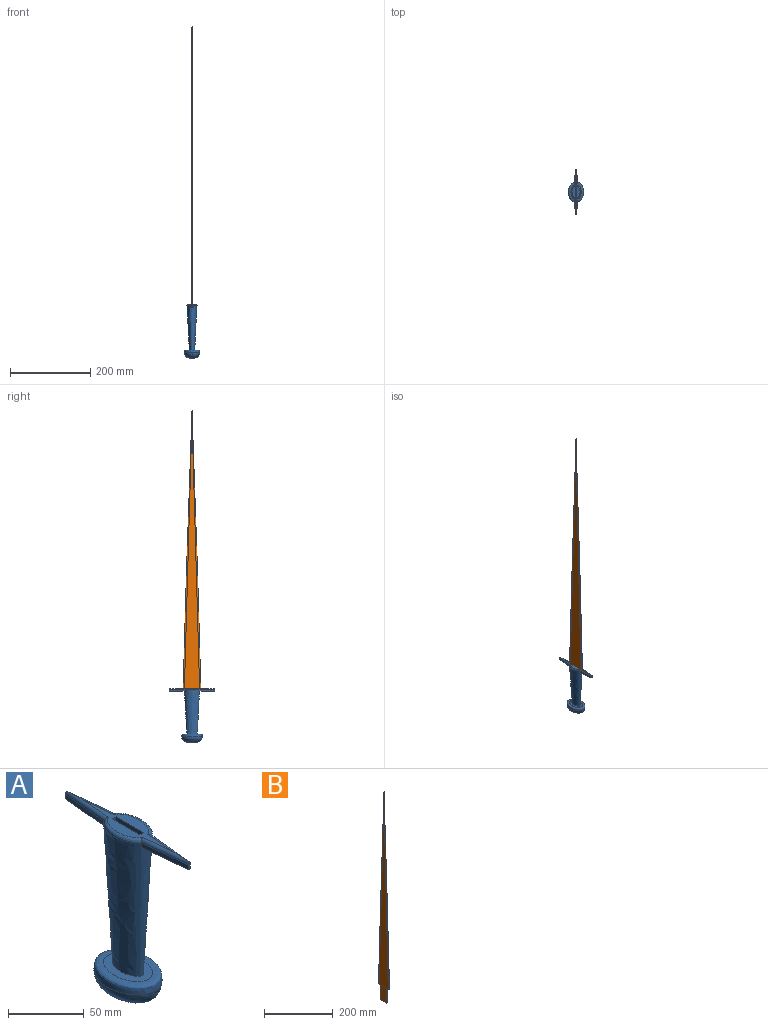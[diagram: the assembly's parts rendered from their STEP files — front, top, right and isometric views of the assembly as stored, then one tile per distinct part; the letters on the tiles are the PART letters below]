
ASSEMBLY  parts=2 mates=1
PART A: 25 faces, bbox 38.4x114.8x133.6 mm
  f0: plane 83.3x20.06mm, normal (0,0,1), area 557mm2, adj f14,f15,f16,f17,f18,f19,f20,f21
  f1: bspline ~111.63x37.8mm, area 9032mm2, adj f3,f7,f8,f9,f10,f11,f12,f16
  f2: plane 25.4x12.71mm, normal (0,0,-1), area 244.5mm2, adj f5
  f3: plane 38.36x25.65mm, normal (0,0,1), area 483.8mm2, adj f1,f4
  f4: bspline ~50.69x38.09mm, area 1476.3mm2, adj f3,f5
  f5: bspline ~50.82x38.12mm, area 2236.3mm2, adj f2,f4
  f6: plane 5.92x2.17mm, normal (0,-1,0), area 11.1mm2, adj f7,f8,f9,f18,f19
  f7: plane 40.12x9.96mm, normal (0,0,-1), area 228.4mm2, adj f1,f6,f8,f9
  f8: plane 39.98x3.85mm, normal (1,-0.1,0), area 152.5mm2, adj f1,f6,f7,f16,f18
  f9: plane 39.98x3.85mm, normal (-1,-0.1,0), area 152.5mm2, adj f1,f6,f7,f17,f19
  f10: plane 40.12x9.97mm, normal (0,0,-1), area 228.4mm2, adj f1,f11,f12,f13
  f11: plane 39.98x3.85mm, normal (-1,0.1,0), area 152.5mm2, adj f1,f10,f13,f15,f17
  f12: plane 39.98x3.85mm, normal (1,0.1,0), area 152.5mm2, adj f1,f10,f13,f14,f16
  f13: plane 5.92x2.17mm, normal (0,1,0), area 11.1mm2, adj f10,f11,f12,f14,f15
  f14: cylinder r=2.54mm len=41.42mm, axis (0.1,-1,0), area 150mm2, adj f0,f12,f13,f15,f16
  f15: cylinder r=2.54mm len=41.42mm, axis (-0.1,-1,0), area 150mm2, adj f0,f11,f13,f14,f17
  f16: bspline ~37.37x11.19mm, area 159.3mm2, adj f0,f1,f8,f12,f14,f18
  f17: bspline ~37.5x11.32mm, area 159.3mm2, adj f0,f1,f9,f11,f15,f19
  f18: cylinder r=2.54mm len=41.42mm, axis (-0.1,-1,0), area 150mm2, adj f0,f6,f8,f16,f19
  f19: cylinder r=2.54mm len=41.42mm, axis (0.1,-1,0), area 150mm2, adj f0,f6,f9,f17,f18
  f20: plane 50.8x3.18mm, normal (0,-1,0), area 161.3mm2, adj f0,f21,f23,f24
  f21: plane 50.8x25.4mm, normal (1,0,0), area 1290.3mm2, adj f0,f20,f22,f24
  f22: plane 50.8x3.18mm, normal (0,1,0), area 161.3mm2, adj f0,f21,f23,f24
  f23: plane 50.8x25.4mm, normal (-1,0,0), area 1290.3mm2, adj f0,f20,f22,f24
  f24: plane 25.4x3.18mm, normal (0,0,1), area 80.6mm2, adj f20,f21,f22,f23
PART B: 15 faces, bbox 3.2x44.2x747.3 mm
  f0: plane 9.4x3.18mm, normal (0,0,-1), area 26.7mm2, adj f1,f2,f3,f6,f8,f12
  f1: plane 675.07x37.89mm, normal (1,0,0), area 12790.7mm2, adj f0,f5,f8,f9,f13
  f2: plane 296.15x8.31mm, normal (0,1,0.03), area 176.1mm2, adj f0,f6,f8
  f3: plane 675.07x37.89mm, normal (-1,0,0), area 12790.7mm2, adj f0,f5,f6,f7,f11
  f4: plane 296.15x8.31mm, normal (0,-1,0.03), area 176.1mm2, adj f5,f7,f9
  f5: plane 9.4x3.18mm, normal (0,0,-1), area 26.7mm2, adj f1,f3,f4,f7,f9,f10
  f6: plane 696.5x22.1mm, normal (-0.95,0.3,0.01), area 1759.2mm2, adj f0,f2,f3,f7,f8
  f7: plane 696.5x22.1mm, normal (-0.95,-0.3,0.01), area 1759.2mm2, adj f3,f4,f5,f6,f9
  f8: plane 696.5x22.1mm, normal (0.95,0.3,0.01), area 1759.2mm2, adj f0,f1,f2,f6,f9
  f9: plane 696.5x22.1mm, normal (0.95,-0.3,0.01), area 1759.2mm2, adj f1,f4,f5,f7,f8
  f10: plane 50.8x3.18mm, normal (0,-1,0), area 161.3mm2, adj f5,f11,f13,f14
  f11: plane 50.8x25.4mm, normal (-1,0,0), area 1290.3mm2, adj f3,f10,f12,f14
  f12: plane 50.8x3.18mm, normal (0,1,0), area 161.3mm2, adj f0,f11,f13,f14
  f13: plane 50.8x25.4mm, normal (1,0,0), area 1290.3mm2, adj f1,f10,f12,f14
  f14: plane 25.4x3.18mm, normal (0,0,-1), area 80.6mm2, adj f10,f11,f12,f13
PLACE A at identity
PLACE B t=(0,0,114.3)mm
MATE fastened B.f14 <-> A.f24  axis (0,0,-1) through (0,0,63.5)mm
